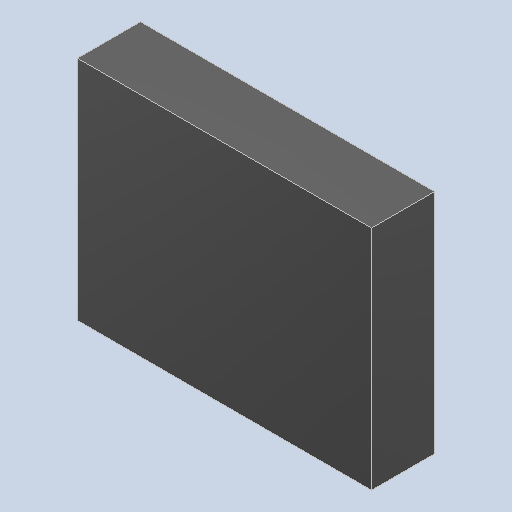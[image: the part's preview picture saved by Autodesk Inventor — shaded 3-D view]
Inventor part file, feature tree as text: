
AUTODESK INVENTOR PART (.ipt)
format: ipt  version: 2023.4 (Build 274418000, 418)  size: 83,456 bytes
history: native  units: mm
features: extrude x1
ambient origin geometry x8: Origin, YZ Plane, XZ Plane, XY Plane, X Axis, Y Axis, Z Axis, Center Point
bodies: Solid1 (feature_tree)
feature tree (1):
  extrude  "Extruded"  [1 undecoded]
note: 1 required parameter value undecoded (feature->parameter linkage not recoverable at this tier; creation-order binding heuristic only, values carry confidence <= 0.55)
